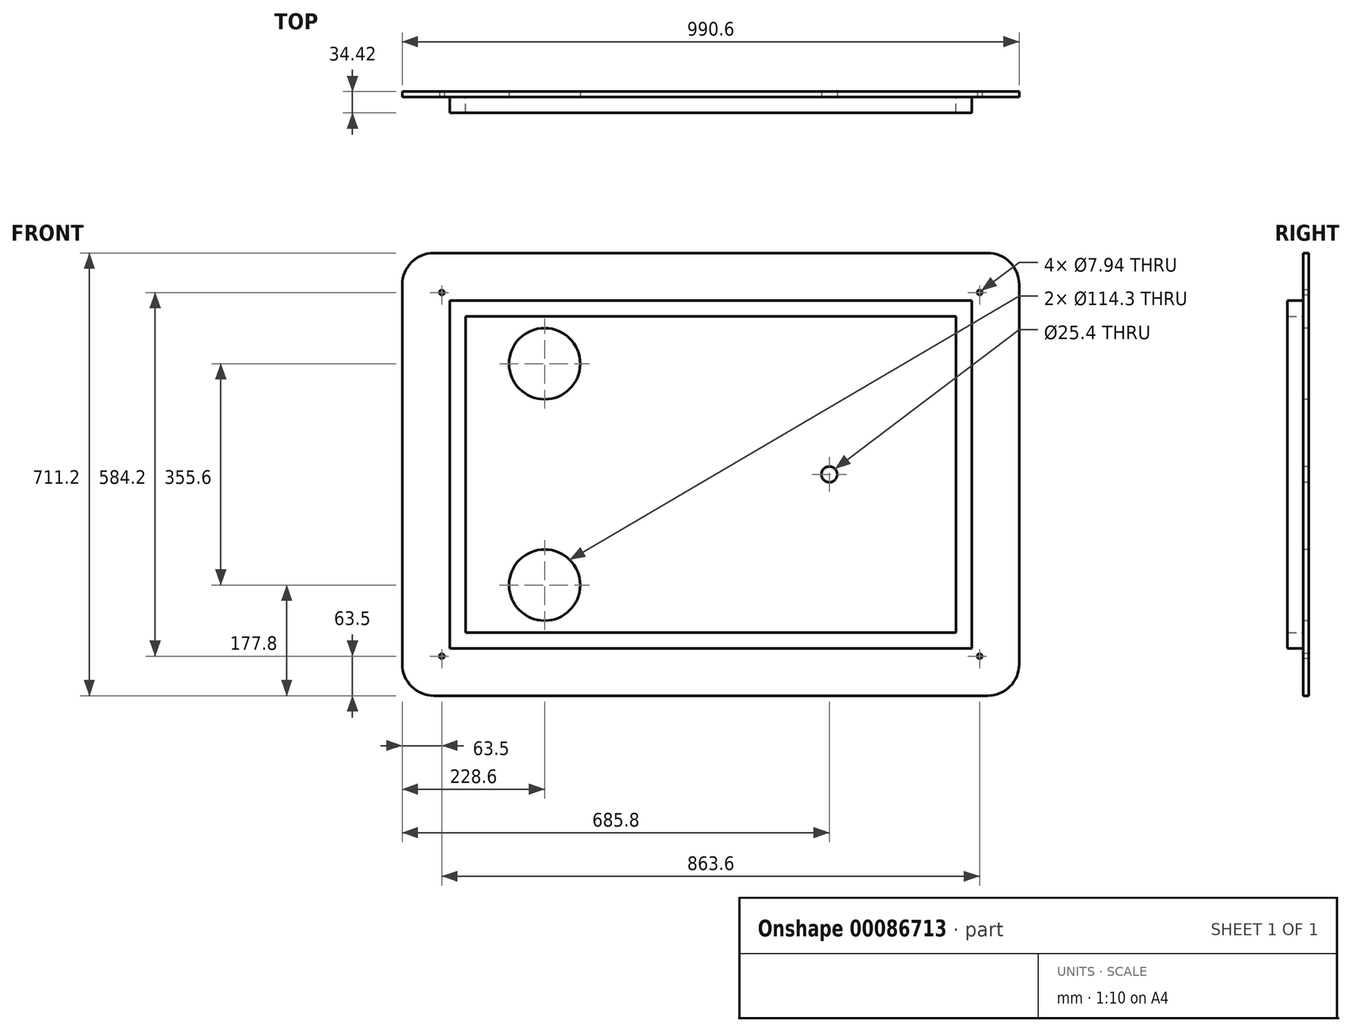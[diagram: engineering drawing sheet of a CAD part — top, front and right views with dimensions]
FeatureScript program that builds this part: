
annotation { "Feature Type Name" : "Feature", "Feature Type Description" : "" }
export const myFeature = defineFeature(function(context is Context, id is Id, definition is map)
    precondition{}
    {
        {
            var Q0;
            Q0=qCreatedBy(makeId("Front.planeOp"),FACE);
            var sketch = newSketch(context, id + "F0", { "sketchPlane" : qUnion([Q0])});
            skLineSegment(sketch, "E0.bottom", {"start": v(-495.3, 355.6) * mm, "end": v(495.3, 355.6) * mm});
            skLineSegment(sketch, "E0.top", {"start": v(-495.3, -355.6) * mm, "end": v(495.3, -355.6) * mm});
            skLineSegment(sketch, "E0.left", {"start": v(-495.3, 355.6) * mm, "end": v(-495.3, -355.6) * mm});
            skLineSegment(sketch, "E0.right", {"start": v(495.3, 355.6) * mm, "end": v(495.3, -355.6) * mm});
            skSolve(sketch);
        }
        {
            var Q0;
            Q0 = qSketchRegion(id + "F0", true);
            extrude(context, id + "F1", {"entities" : qUnion([Q0]), "oppositeDirection" : true, "depth" : 9.02 * mm});
        }
        {
            var Q0;
            Q0=makeQuery(id+"F1.opExtrude","SWEPT_EDGE",EDGE,{"disambiguationData":[OSD([sQuery(id+"F0.wireOp",EDGE,"E0.bottom"),sQuery(id+"F0.wireOp",EDGE,"E0.right")])]});
            var Q1;
            Q1=makeQuery(id+"F1.opExtrude","SWEPT_EDGE",EDGE,{"disambiguationData":[OSD([sQuery(id+"F0.wireOp",EDGE,"E0.top"),sQuery(id+"F0.wireOp",EDGE,"E0.right")])]});
            var Q2;
            Q2=makeQuery(id+"F1.opExtrude","SWEPT_EDGE",EDGE,{"disambiguationData":[OSD([sQuery(id+"F0.wireOp",EDGE,"E0.top"),sQuery(id+"F0.wireOp",EDGE,"E0.left")])]});
            var Q3;
            Q3=makeQuery(id+"F1.opExtrude","SWEPT_EDGE",EDGE,{"disambiguationData":[OSD([sQuery(id+"F0.wireOp",EDGE,"E0.bottom"),sQuery(id+"F0.wireOp",EDGE,"E0.left")])]});
            fillet(context, id + "F2", {"entities" : qUnion([Q0, Q1, Q2, Q3]), "radius" : 50.8 * mm, "tangentPropagation" : true, "allowEdgeOverflow" : false});
        }
        {
            var Q0;
            Q0=qCreatedBy(makeId("Front.planeOp"),FACE);
            var sketch = newSketch(context, id + "F3", { "sketchPlane" : qUnion([Q0])});
            skLineSegment(sketch, "E1.bottom", {"start": v(-431.8, 292.1) * mm, "end": v(431.8, 292.1) * mm, "construction": true});
            skLineSegment(sketch, "E1.top", {"start": v(-431.8, -292.1) * mm, "end": v(431.8, -292.1) * mm, "construction": true});
            skLineSegment(sketch, "E1.left", {"start": v(-431.8, 292.1) * mm, "end": v(-431.8, -292.1) * mm, "construction": true});
            skLineSegment(sketch, "E1.right", {"start": v(431.8, 292.1) * mm, "end": v(431.8, -292.1) * mm, "construction": true});
            skCircle(sketch, "E2", {"center": v(-431.8, 292.1) * mm, "radius": 3.97 * mm});
            skCircle(sketch, "E3", {"center": v(431.8, 292.1) * mm, "radius": 3.97 * mm});
            skCircle(sketch, "E4", {"center": v(431.8, -292.1) * mm, "radius": 3.97 * mm});
            skCircle(sketch, "E5", {"center": v(-431.8, -292.1) * mm, "radius": 3.97 * mm});
            skSolve(sketch);
        }
        {
            var Q0;
            Q0 = qSketchRegion(id + "F3", true);
            extrude(context, id + "F4", {"entities" : qUnion([Q0]), "operationType" : NewBodyOperationType.REMOVE, "endBound" : BoundingType.THROUGH_ALL, "oppositeDirection" : true, "depth" : 25.4 * mm});
        }
        {
            var Q0;
            Q0=qCreatedBy(makeId("Front.planeOp"),FACE);
            var sketch = newSketch(context, id + "F5", { "sketchPlane" : qUnion([Q0])});
            skCircle(sketch, "E6", {"center": v(190.5, 0) * mm, "radius": 12.7 * mm});
            skSolve(sketch);
        }
        {
            var Q0;
            Q0 = qSketchRegion(id + "F5", true);
            extrude(context, id + "F6", {"entities" : qUnion([Q0]), "operationType" : NewBodyOperationType.REMOVE, "endBound" : BoundingType.THROUGH_ALL, "oppositeDirection" : true, "depth" : 25.4 * mm});
        }
        {
            var Q0;
            Q0=qCreatedBy(makeId("Front.planeOp"),FACE);
            var sketch = newSketch(context, id + "F7", { "sketchPlane" : qUnion([Q0])});
            skLineSegment(sketch, "E7.bottom", {"start": v(-419.1, 279.4) * mm, "end": v(419.1, 279.4) * mm});
            skLineSegment(sketch, "E7.top", {"start": v(-419.1, -279.4) * mm, "end": v(419.1, -279.4) * mm});
            skLineSegment(sketch, "E7.left", {"start": v(-419.1, 279.4) * mm, "end": v(-419.1, -279.4) * mm});
            skLineSegment(sketch, "E7.right", {"start": v(419.1, 279.4) * mm, "end": v(419.1, -279.4) * mm});
            skLineSegment(sketch, "E8.bottom", {"start": v(-393.7, 254) * mm, "end": v(393.7, 254) * mm});
            skLineSegment(sketch, "E8.top", {"start": v(-393.7, -254) * mm, "end": v(393.7, -254) * mm});
            skLineSegment(sketch, "E8.left", {"start": v(-393.7, 254) * mm, "end": v(-393.7, -254) * mm});
            skLineSegment(sketch, "E8.right", {"start": v(393.7, 254) * mm, "end": v(393.7, -254) * mm});
            skSolve(sketch);
        }
        {
            var Q0;
            Q0 = qSketchRegion(id + "F7", true);
            extrude(context, id + "F8", {"entities" : qUnion([Q0]), "operationType" : NewBodyOperationType.ADD, "depth" : 25.4 * mm});
        }
        {
            var Q0;
            Q0=qCreatedBy(makeId("Front.planeOp"),FACE);
            var sketch = newSketch(context, id + "F9", { "sketchPlane" : qUnion([Q0])});
            skCircle(sketch, "E9", {"center": v(-266.7, 177.8) * mm, "radius": 57.15 * mm});
            skCircle(sketch, "E10", {"center": v(-266.7, -177.8) * mm, "radius": 57.15 * mm});
            skLineSegment(sketch, "E11", {"start": v(-266.7, 177.8) * mm, "end": v(-266.7, -177.8) * mm, "construction": true});
            skSolve(sketch);
        }
        {
            var Q0;
            Q0 = qSketchRegion(id + "F9", true);
            extrude(context, id + "F10", {"entities" : qUnion([Q0]), "operationType" : NewBodyOperationType.REMOVE, "endBound" : BoundingType.THROUGH_ALL, "oppositeDirection" : true, "depth" : 25.4 * mm});
        }
    });
